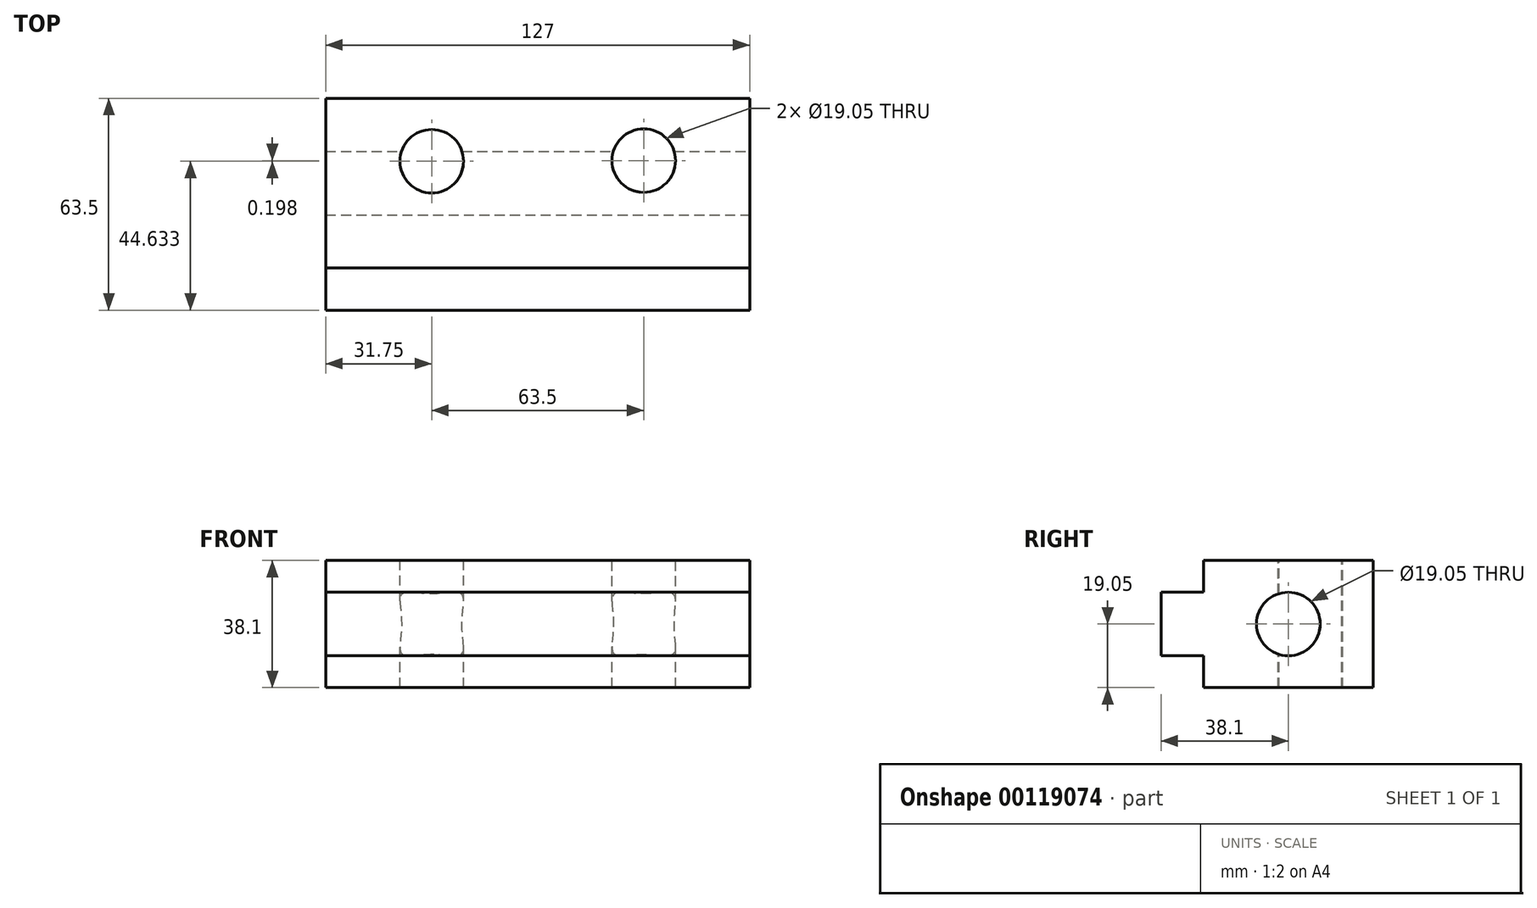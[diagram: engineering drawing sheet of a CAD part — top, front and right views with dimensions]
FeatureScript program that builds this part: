
annotation { "Feature Type Name" : "Feature", "Feature Type Description" : "" }
export const myFeature = defineFeature(function(context is Context, id is Id, definition is map)
    precondition{}
    {
        {
            var Q0;
            Q0=qCreatedBy(makeId("Top.planeOp"),FACE);
            var sketch = newSketch(context, id + "F0", { "sketchPlane" : qUnion([Q0])});
            skLineSegment(sketch, "E0.bottom", {"start": v(0, 0) * mm, "end": v(127, 0) * mm});
            skLineSegment(sketch, "E0.top", {"start": v(0, -63.5) * mm, "end": v(127, -63.5) * mm});
            skLineSegment(sketch, "E0.left", {"start": v(0, 0) * mm, "end": v(0, -63.5) * mm});
            skLineSegment(sketch, "E0.right", {"start": v(127, 0) * mm, "end": v(127, -63.5) * mm});
            skSolve(sketch);
        }
        {
            var Q0;
            Q0 = qSketchRegion(id + "F0", true);
            extrude(context, id + "F1", {"entities" : qUnion([Q0]), "depth" : 38.1 * mm});
        }
        {
            var Q0;
            Q0=makeQuery(id+"F1.opExtrude","SWEPT_FACE",FACE,{"disambiguationData":[OSD([sQuery(id+"F0.wireOp",EDGE,"E0.right")])]});
            var sketch = newSketch(context, id + "F2", { "sketchPlane" : qUnion([Q0])});
            skLineSegment(sketch, "E1.bottom", {"start": v(-63.5, 38.1) * mm, "end": v(-50.8, 38.1) * mm});
            skLineSegment(sketch, "E1.top", {"start": v(-63.5, 28.58) * mm, "end": v(-50.8, 28.58) * mm});
            skLineSegment(sketch, "E1.left", {"start": v(-63.5, 38.1) * mm, "end": v(-63.5, 28.58) * mm});
            skLineSegment(sketch, "E1.right", {"start": v(-50.8, 38.1) * mm, "end": v(-50.8, 28.58) * mm});
            skLineSegment(sketch, "E2.bottom", {"start": v(-63.5, 0) * mm, "end": v(-50.8, 0) * mm});
            skLineSegment(sketch, "E2.top", {"start": v(-63.5, 9.53) * mm, "end": v(-50.8, 9.53) * mm});
            skLineSegment(sketch, "E2.left", {"start": v(-63.5, 0) * mm, "end": v(-63.5, 9.53) * mm});
            skLineSegment(sketch, "E2.right", {"start": v(-50.8, 0) * mm, "end": v(-50.8, 9.53) * mm});
            skSolve(sketch);
        }
        {
            var Q0;
            Q0 = qSketchRegion(id + "F2", true);
            extrude(context, id + "F3", {"entities" : qUnion([Q0]), "operationType" : NewBodyOperationType.REMOVE, "oppositeDirection" : true, "depth" : 127 * mm});
        }
        {
            var Q0;
            Q0=makeQuery(id+"F1.opExtrude","CAP_FACE",FACE,{"disambiguationData":[OSD([sQuery(id+"F0.wireOp",EDGE,"E0.bottom"),sQuery(id+"F0.wireOp",EDGE,"E0.top"),sQuery(id+"F0.wireOp",EDGE,"E0.left"),sQuery(id+"F0.wireOp",EDGE,"E0.right")])],"isStart":false});
            var sketch = newSketch(context, id + "F4", { "sketchPlane" : qUnion([Q0])});
            skCircle(sketch, "E3", {"center": v(31.75, -18.87) * mm, "radius": 9.53 * mm});
            skCircle(sketch, "E4", {"center": v(95.25, -18.67) * mm, "radius": 9.53 * mm});
            skSolve(sketch);
        }
        {
            var Q0;
            Q0 = qSketchRegion(id + "F4", true);
            extrude(context, id + "F5", {"entities" : qUnion([Q0]), "operationType" : NewBodyOperationType.ADD, "depth" : 25.4 * mm});
        }
        {
            var Q0;
            Q0=makeQuery(id+"F5.opExtrude","CAP_FACE",FACE,{"disambiguationData":[OSD([sQuery(id+"F4.wireOp",EDGE,"E3")])],"isStart":false});
            var Q1;
            Q1=makeQuery(id+"F5.opExtrude","CAP_FACE",FACE,{"disambiguationData":[OSD([sQuery(id+"F4.wireOp",EDGE,"E4")])],"isStart":false});
            extrude(context, id + "F6", {"entities" : qUnion([Q0, Q1]), "operationType" : NewBodyOperationType.REMOVE, "oppositeDirection" : true, "depth" : 63.8 * mm});
        }
        {
            var Q0;
            Q0=makeQuery(id+"F1.opExtrude","SWEPT_FACE",FACE,{"disambiguationData":[OSD([sQuery(id+"F0.wireOp",EDGE,"E0.right")])]});
            var sketch = newSketch(context, id + "F7", { "sketchPlane" : qUnion([Q0])});
            skCircle(sketch, "E5", {"center": v(-25.4, 19.05) * mm, "radius": 9.53 * mm});
            skSolve(sketch);
        }
        {
            var Q0;
            Q0 = qSketchRegion(id + "F7", true);
            extrude(context, id + "F8", {"entities" : qUnion([Q0]), "operationType" : NewBodyOperationType.REMOVE, "oppositeDirection" : true, "depth" : 127.3 * mm});
        }
    });
